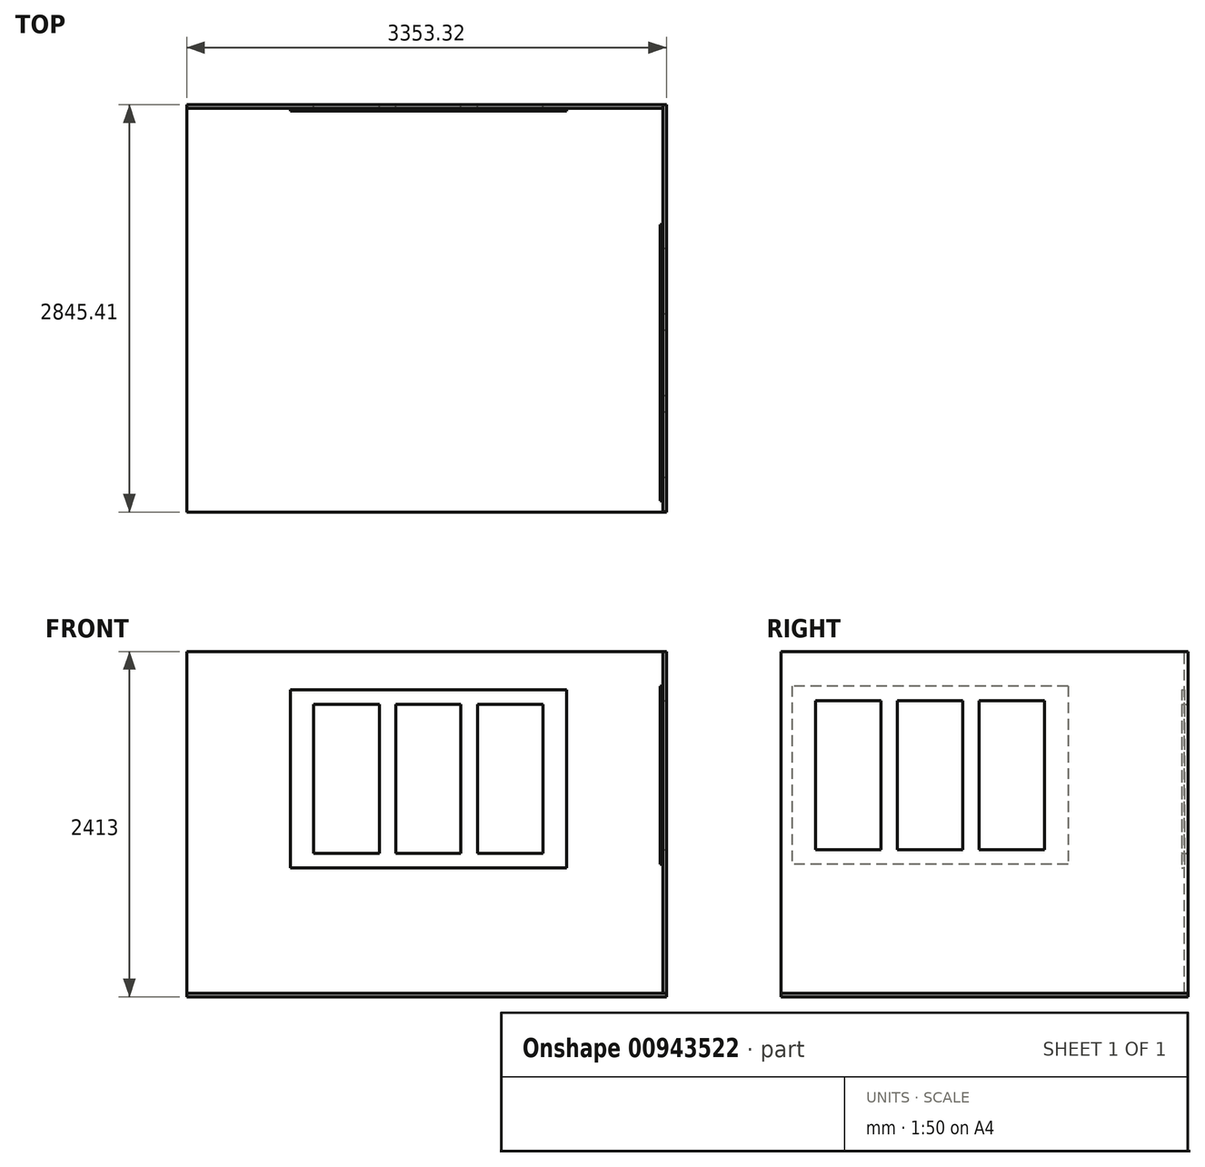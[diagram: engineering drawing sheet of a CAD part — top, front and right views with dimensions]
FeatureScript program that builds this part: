
annotation { "Feature Type Name" : "Feature", "Feature Type Description" : "" }
export const myFeature = defineFeature(function(context is Context, id is Id, definition is map)
    precondition{}
    {
        {
            var Q0;
            Q0=qCreatedBy(makeId("Front.planeOp"),FACE);
            var sketch = newSketch(context, id + "F0", { "sketchPlane" : qUnion([Q0])});
            skLineSegment(sketch, "E0.bottom", {"start": v(0, 0) * mm, "end": v(3327.4, 0) * mm});
            skLineSegment(sketch, "E0.top", {"start": v(0, 2387.6) * mm, "end": v(3327.4, 2387.6) * mm});
            skLineSegment(sketch, "E0.left", {"start": v(0, 0) * mm, "end": v(0, 2387.6) * mm});
            skLineSegment(sketch, "E0.right", {"start": v(3327.4, 0) * mm, "end": v(3327.4, 2387.6) * mm});
            skSolve(sketch);
        }
        {
            var Q0;
            Q0=makeQuery(id+"F0.imprint","IMPRINT",FACE,{"disambiguationData":[TD([[makeQuery(id+"F0.imprint","IMPRINT",EDGE,{"derivedFrom":sQuery(id+"F0.wireOp",EDGE,"E0.bottom")}),1.0]])]});
            extrude(context, id + "F1", {"entities" : qUnion([Q0]), "depth" : 25.4 * mm, "offsetDistance" : 25.4 * mm});
        }
        {
            var Q0;
            Q0=makeQuery(id+"F1.opExtrude","CAP_FACE",FACE,{"disambiguationData":[OSD([sQuery(id+"F0.wireOp",EDGE,"E0.bottom"),sQuery(id+"F0.wireOp",EDGE,"E0.top"),sQuery(id+"F0.wireOp",EDGE,"E0.left"),sQuery(id+"F0.wireOp",EDGE,"E0.right")])],"isStart":false});
            var sketch = newSketch(context, id + "F2", { "sketchPlane" : qUnion([Q0])});
            skLineSegment(sketch, "E1.bottom", {"start": v(723.9, 2120.9) * mm, "end": v(2654.3, 2120.9) * mm});
            skLineSegment(sketch, "E1.top", {"start": v(723.9, 876.3) * mm, "end": v(2654.3, 876.3) * mm});
            skLineSegment(sketch, "E1.left", {"start": v(723.9, 2120.9) * mm, "end": v(723.9, 876.3) * mm});
            skLineSegment(sketch, "E1.right", {"start": v(2654.3, 2120.9) * mm, "end": v(2654.3, 876.3) * mm});
            skLineSegment(sketch, "E2.bottom", {"start": v(889, 2019.3) * mm, "end": v(1346.2, 2019.3) * mm});
            skLineSegment(sketch, "E2.top", {"start": v(889, 977.9) * mm, "end": v(1346.2, 977.9) * mm});
            skLineSegment(sketch, "E2.left", {"start": v(889, 2019.3) * mm, "end": v(889, 977.9) * mm});
            skLineSegment(sketch, "E2.right", {"start": v(1346.2, 2019.3) * mm, "end": v(1346.2, 977.9) * mm});
            skLineSegment(sketch, "E3.1.0.0", {"start": v(1917.7, 2019.3) * mm, "end": v(1917.7, 977.9) * mm});
            skLineSegment(sketch, "E3.1.0.1", {"start": v(1460.5, 2019.3) * mm, "end": v(1917.7, 2019.3) * mm});
            skLineSegment(sketch, "E3.1.0.2", {"start": v(1460.5, 2019.3) * mm, "end": v(1460.5, 977.9) * mm});
            skLineSegment(sketch, "E3.1.0.3", {"start": v(1460.5, 977.9) * mm, "end": v(1917.7, 977.9) * mm});
            skLineSegment(sketch, "E3.2.0.0", {"start": v(2489.2, 2019.3) * mm, "end": v(2489.2, 977.9) * mm});
            skLineSegment(sketch, "E3.2.0.1", {"start": v(2032, 2019.3) * mm, "end": v(2489.2, 2019.3) * mm});
            skLineSegment(sketch, "E3.2.0.2", {"start": v(2032, 2019.3) * mm, "end": v(2032, 977.9) * mm});
            skLineSegment(sketch, "E3.2.0.3", {"start": v(2032, 977.9) * mm, "end": v(2489.2, 977.9) * mm});
            skLineSegment(sketch, "E3.direction1", {"start": v(1346.2, 977.9) * mm, "end": v(1917.7, 977.9) * mm, "construction": true});
            skSolve(sketch);
        }
        {
            var Q0;
            Q0=makeQuery(id+"F2.imprint","IMPRINT",FACE,{"disambiguationData":[TD([[makeQuery(id+"F2.imprint","IMPRINT",EDGE,{"derivedFrom":sQuery(id+"F2.wireOp",EDGE,"E1.bottom")}),-1.0]])]});
            extrude(context, id + "F3", {"entities" : qUnion([Q0]), "operationType" : NewBodyOperationType.ADD, "depth" : 19.05 * mm, "offsetDistance" : 25.4 * mm});
        }
        {
            var Q0;
            Q0=makeQuery(id+"F3.boolean.opBoolean","SPLIT",FACE,{"disambiguationData":[TD([makeQuery(id+"F3.opExtrude","SWEPT_FACE",FACE,{"disambiguationData":[OSD([sQuery(id+"F2.wireOp",EDGE,"E2.bottom")])]})])],"derivedFrom":makeQuery(id+"F1.opExtrude","CAP_FACE",FACE,{"disambiguationData":[OSD([sQuery(id+"F0.wireOp",EDGE,"E0.bottom"),sQuery(id+"F0.wireOp",EDGE,"E0.top"),sQuery(id+"F0.wireOp",EDGE,"E0.left"),sQuery(id+"F0.wireOp",EDGE,"E0.right")])],"isStart":false})});
            var Q1;
            Q1=makeQuery(id+"F3.boolean.opBoolean","SPLIT",FACE,{"disambiguationData":[TD([makeQuery(id+"F3.opExtrude","SWEPT_FACE",FACE,{"disambiguationData":[OSD([sQuery(id+"F2.wireOp",EDGE,"E3.1.0.0")])]})])],"derivedFrom":makeQuery(id+"F1.opExtrude","CAP_FACE",FACE,{"disambiguationData":[OSD([sQuery(id+"F0.wireOp",EDGE,"E0.bottom"),sQuery(id+"F0.wireOp",EDGE,"E0.top"),sQuery(id+"F0.wireOp",EDGE,"E0.left"),sQuery(id+"F0.wireOp",EDGE,"E0.right")])],"isStart":false})});
            var Q2;
            Q2=makeQuery(id+"F3.boolean.opBoolean","SPLIT",FACE,{"disambiguationData":[TD([makeQuery(id+"F3.opExtrude","SWEPT_FACE",FACE,{"disambiguationData":[OSD([sQuery(id+"F2.wireOp",EDGE,"E3.2.0.0")])]})])],"derivedFrom":makeQuery(id+"F1.opExtrude","CAP_FACE",FACE,{"disambiguationData":[OSD([sQuery(id+"F0.wireOp",EDGE,"E0.bottom"),sQuery(id+"F0.wireOp",EDGE,"E0.top"),sQuery(id+"F0.wireOp",EDGE,"E0.left"),sQuery(id+"F0.wireOp",EDGE,"E0.right")])],"isStart":false})});
            extrude(context, id + "F4", {"entities" : qUnion([Q0, Q1, Q2]), "operationType" : NewBodyOperationType.REMOVE, "oppositeDirection" : true, "depth" : 25.4 * mm, "offsetDistance" : 25.4 * mm});
        }
        {
            var Q0;
            Q0=makeQuery(id+"F1.opExtrude","SWEPT_FACE",FACE,{"disambiguationData":[OSD([sQuery(id+"F0.wireOp",EDGE,"E0.right")])]});
            cPlane(context, id + "F5", {"entities" : qUnion([Q0]), "cplaneType" : CPlaneType.OFFSET, "offset" : 25.4 * mm, "width" : 152.4 * mm, "height" : 152.4 * mm});
        }
        {
            var Q0;
            Q0=qCreatedBy(id+"F5.planeOp",FACE);
            var sketch = newSketch(context, id + "F6", { "sketchPlane" : qUnion([Q0])});
            skLineSegment(sketch, "E4.bottom", {"start": v(0, 0) * mm, "end": v(-2844.8, 0) * mm});
            skLineSegment(sketch, "E4.top", {"start": v(0, 2387.6) * mm, "end": v(-2844.8, 2387.6) * mm});
            skLineSegment(sketch, "E4.left", {"start": v(0, 0) * mm, "end": v(0, 2387.6) * mm});
            skLineSegment(sketch, "E4.right", {"start": v(-2844.8, 0) * mm, "end": v(-2844.8, 2387.6) * mm});
            skSolve(sketch);
        }
        {
            var Q0;
            Q0=makeQuery(id+"F6.imprint","IMPRINT",FACE,{"disambiguationData":[TD([[makeQuery(id+"F6.imprint","IMPRINT",EDGE,{"derivedFrom":sQuery(id+"F6.wireOp",EDGE,"E4.bottom")}),-1.0]])]});
            extrude(context, id + "F7", {"entities" : qUnion([Q0]), "oppositeDirection" : true, "depth" : 25.4 * mm, "offsetDistance" : 25.4 * mm});
        }
        {
            var Q0;
            Q0=makeQuery(id+"F7.opExtrude","CAP_FACE",FACE,{"disambiguationData":[OSD([sQuery(id+"F6.wireOp",EDGE,"E4.bottom"),sQuery(id+"F6.wireOp",EDGE,"E4.top"),sQuery(id+"F6.wireOp",EDGE,"E4.left"),sQuery(id+"F6.wireOp",EDGE,"E4.right")])],"isStart":false});
            var sketch = newSketch(context, id + "F8", { "sketchPlane" : qUnion([Q0])});
            skLineSegment(sketch, "E5.bottom", {"start": v(838.2, 2146.3) * mm, "end": v(2768.6, 2146.3) * mm});
            skLineSegment(sketch, "E5.top", {"start": v(838.2, 901.7) * mm, "end": v(2768.6, 901.7) * mm});
            skLineSegment(sketch, "E5.left", {"start": v(838.2, 2146.3) * mm, "end": v(838.2, 901.7) * mm});
            skLineSegment(sketch, "E5.right", {"start": v(2768.6, 2146.3) * mm, "end": v(2768.6, 901.7) * mm});
            skLineSegment(sketch, "E6.bottom", {"start": v(1003.3, 2044.7) * mm, "end": v(1460.5, 2044.7) * mm});
            skLineSegment(sketch, "E6.top", {"start": v(1003.3, 1003.3) * mm, "end": v(1460.5, 1003.3) * mm});
            skLineSegment(sketch, "E6.left", {"start": v(1003.3, 2044.7) * mm, "end": v(1003.3, 1003.3) * mm});
            skLineSegment(sketch, "E6.right", {"start": v(1460.5, 2044.7) * mm, "end": v(1460.5, 1003.3) * mm});
            skLineSegment(sketch, "E7.1.0.0", {"start": v(2032, 2044.7) * mm, "end": v(2032, 1003.3) * mm});
            skLineSegment(sketch, "E7.1.0.1", {"start": v(1574.8, 2044.7) * mm, "end": v(2032, 2044.7) * mm});
            skLineSegment(sketch, "E7.1.0.2", {"start": v(1574.8, 2044.7) * mm, "end": v(1574.8, 1003.3) * mm});
            skLineSegment(sketch, "E7.1.0.3", {"start": v(1574.8, 1003.3) * mm, "end": v(2032, 1003.3) * mm});
            skLineSegment(sketch, "E7.1.0.4", {"start": v(1409.7, 901.7) * mm, "end": v(3340.1, 901.7) * mm});
            skLineSegment(sketch, "E7.2.0.0", {"start": v(2603.5, 2044.7) * mm, "end": v(2603.5, 1003.3) * mm});
            skLineSegment(sketch, "E7.2.0.1", {"start": v(2146.3, 2044.7) * mm, "end": v(2603.5, 2044.7) * mm});
            skLineSegment(sketch, "E7.2.0.2", {"start": v(2146.3, 2044.7) * mm, "end": v(2146.3, 1003.3) * mm});
            skLineSegment(sketch, "E7.2.0.3", {"start": v(2146.3, 1003.3) * mm, "end": v(2603.5, 1003.3) * mm});
            skLineSegment(sketch, "E7.2.0.4", {"start": v(1981.2, 901.7) * mm, "end": v(3911.6, 901.7) * mm});
            skLineSegment(sketch, "E7.direction1", {"start": v(1460.5, 1003.3) * mm, "end": v(2032, 1003.3) * mm, "construction": true});
            skSolve(sketch);
        }
        {
            var Q0;
            Q0=makeQuery(id+"F8.imprint","IMPRINT",FACE,{"disambiguationData":[TD([[makeQuery(id+"F8.imprint","IMPRINT",EDGE,{"derivedFrom":sQuery(id+"F8.wireOp",EDGE,"E5.bottom")}),-1.0]])]});
            extrude(context, id + "F9", {"entities" : qUnion([Q0]), "operationType" : NewBodyOperationType.ADD, "depth" : 19.05 * mm, "offsetDistance" : 25.4 * mm});
        }
        {
            var Q0;
            Q0=makeQuery(id+"F9.boolean.opBoolean","SPLIT",FACE,{"disambiguationData":[TD([makeQuery(id+"F9.opExtrude","SWEPT_FACE",FACE,{"disambiguationData":[OSD([sQuery(id+"F8.wireOp",EDGE,"E6.bottom")])]})])],"derivedFrom":makeQuery(id+"F7.opExtrude","CAP_FACE",FACE,{"disambiguationData":[OSD([sQuery(id+"F6.wireOp",EDGE,"E4.bottom"),sQuery(id+"F6.wireOp",EDGE,"E4.top"),sQuery(id+"F6.wireOp",EDGE,"E4.left"),sQuery(id+"F6.wireOp",EDGE,"E4.right")])],"isStart":false})});
            var Q1;
            Q1=makeQuery(id+"F9.boolean.opBoolean","SPLIT",FACE,{"disambiguationData":[TD([makeQuery(id+"F9.opExtrude","SWEPT_FACE",FACE,{"disambiguationData":[OSD([sQuery(id+"F8.wireOp",EDGE,"E7.1.0.0")])]})])],"derivedFrom":makeQuery(id+"F7.opExtrude","CAP_FACE",FACE,{"disambiguationData":[OSD([sQuery(id+"F6.wireOp",EDGE,"E4.bottom"),sQuery(id+"F6.wireOp",EDGE,"E4.top"),sQuery(id+"F6.wireOp",EDGE,"E4.left"),sQuery(id+"F6.wireOp",EDGE,"E4.right")])],"isStart":false})});
            var Q2;
            Q2=makeQuery(id+"F9.boolean.opBoolean","SPLIT",FACE,{"disambiguationData":[TD([makeQuery(id+"F9.opExtrude","SWEPT_FACE",FACE,{"disambiguationData":[OSD([sQuery(id+"F8.wireOp",EDGE,"E7.2.0.0")])]})])],"derivedFrom":makeQuery(id+"F7.opExtrude","CAP_FACE",FACE,{"disambiguationData":[OSD([sQuery(id+"F6.wireOp",EDGE,"E4.bottom"),sQuery(id+"F6.wireOp",EDGE,"E4.top"),sQuery(id+"F6.wireOp",EDGE,"E4.left"),sQuery(id+"F6.wireOp",EDGE,"E4.right")])],"isStart":false})});
            extrude(context, id + "F10", {"entities" : qUnion([Q0, Q1, Q2]), "operationType" : NewBodyOperationType.REMOVE, "oppositeDirection" : true, "depth" : 25.4 * mm, "offsetDistance" : 25.4 * mm});
        }
        {
            var Q0;
            Q0=qCreatedBy(makeId("Top.planeOp"),FACE);
            var sketch = newSketch(context, id + "F11", { "sketchPlane" : qUnion([Q0])});
            skLineSegment(sketch, "E8.bottom", {"start": v(0, 0) * mm, "end": v(3353.32, 0) * mm});
            skLineSegment(sketch, "E8.top", {"start": v(0, -2845.4) * mm, "end": v(3353.32, -2845.4) * mm});
            skLineSegment(sketch, "E8.left", {"start": v(0, 0) * mm, "end": v(0, -2845.4) * mm});
            skLineSegment(sketch, "E8.right", {"start": v(3353.32, 0) * mm, "end": v(3353.32, -2845.4) * mm});
            skSolve(sketch);
        }
        {
            var Q0;
            Q0=makeQuery(id+"F11.imprint","IMPRINT",FACE,{"disambiguationData":[TD([[makeQuery(id+"F11.imprint","IMPRINT",EDGE,{"derivedFrom":sQuery(id+"F11.wireOp",EDGE,"E8.bottom")}),-1.0]])]});
            extrude(context, id + "F12", {"entities" : qUnion([Q0]), "oppositeDirection" : true, "depth" : 25.4 * mm, "offsetDistance" : 25.4 * mm});
        }
    });
